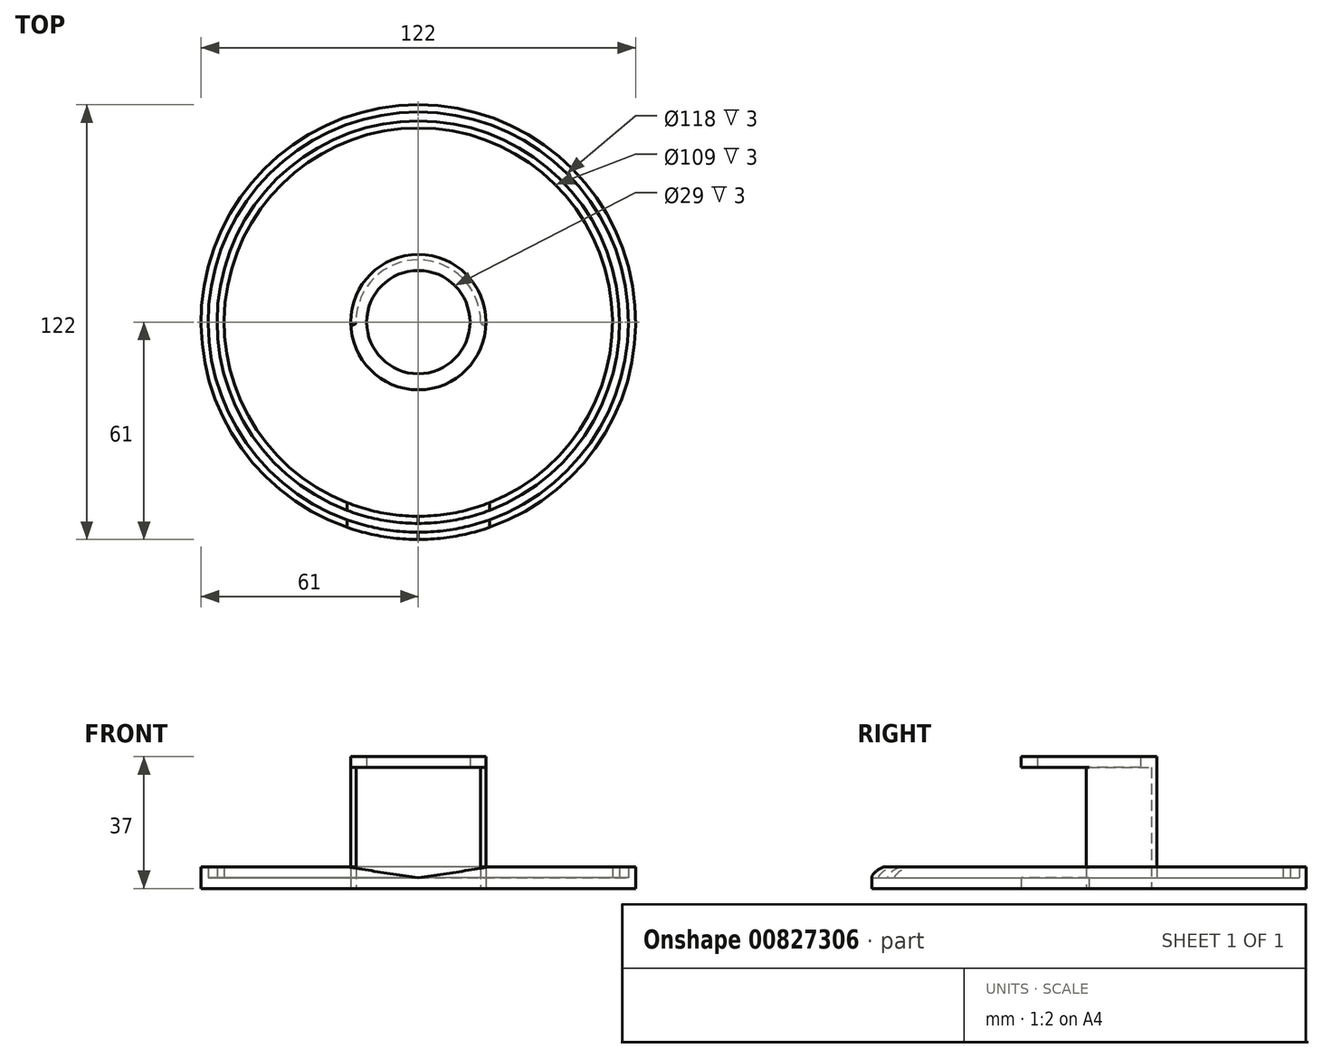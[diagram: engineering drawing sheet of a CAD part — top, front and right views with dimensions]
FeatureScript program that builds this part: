
annotation { "Feature Type Name" : "Feature", "Feature Type Description" : "" }
export const myFeature = defineFeature(function(context is Context, id is Id, definition is map)
    precondition{}
    {
        {
            var Q0;
            Q0=qCreatedBy(makeId("Top.planeOp"),FACE);
            var sketch = newSketch(context, id + "F0", { "sketchPlane" : qUnion([Q0])});
            skCircle(sketch, "E0", {"center": v(0, 0) * mm, "radius": 61 * mm});
            skCircle(sketch, "E1", {"center": v(0, 0) * mm, "radius": 11.5 * mm});
            skCircle(sketch, "E2", {"center": v(0, 0) * mm, "radius": 17.5 * mm});
            skCircle(sketch, "E3", {"center": v(0, 0) * mm, "radius": 14.5 * mm});
            skCircle(sketch, "E4", {"center": v(-18.25, 0) * mm, "radius": 0.75 * mm});
            skCircle(sketch, "E5", {"center": v(18.25, 0) * mm, "radius": 0.75 * mm});
            skCircle(sketch, "E6", {"center": v(0, 0) * mm, "radius": 19 * mm});
            skCircle(sketch, "E7", {"center": v(0, 0) * mm, "radius": 59 * mm});
            skCircle(sketch, "E8", {"center": v(0, 0) * mm, "radius": 56.5 * mm});
            skCircle(sketch, "E9", {"center": v(0, 0) * mm, "radius": 54.5 * mm});
            skSolve(sketch);
        }
        {
            var Q0;
            {var subQ0=sQuery(id+"F0.wireOp",EDGE,"E4");var subQ1=sQuery(id+"F0.wireOp",EDGE,"E2");var subQ2=makeQuery(id+"F0.imprint","INTERSECT",VERTEX,{"derivedFrom":[subQ1,subQ0]});Q0=makeQuery(id+"F0.imprint","IMPRINT",FACE,{"disambiguationData":[TD([[makeQuery(id+"F0.imprint","IMPRINT",EDGE,{"disambiguationData":[TD([[subQ2,1.0]])],"derivedFrom":subQ1}),-1.0]])]});}
            var Q1;
            {var subQ0=sQuery(id+"F0.wireOp",EDGE,"E5");var subQ1=makeQuery(id+"F0.imprint","INTERSECT",VERTEX,{"derivedFrom":[sQuery(id+"F0.wireOp",EDGE,"E2"),subQ0]});Q1=makeQuery(id+"F0.imprint","IMPRINT",FACE,{"disambiguationData":[TD([[makeQuery(id+"F0.imprint","IMPRINT",EDGE,{"disambiguationData":[TD([[subQ1,1.0]])],"derivedFrom":subQ0}),1.0]])]});}
            var Q2;
            {var subQ0=sQuery(id+"F0.wireOp",EDGE,"E4");var subQ1=makeQuery(id+"F0.imprint","INTERSECT",VERTEX,{"derivedFrom":[sQuery(id+"F0.wireOp",EDGE,"E2"),subQ0]});Q2=makeQuery(id+"F0.imprint","IMPRINT",FACE,{"disambiguationData":[TD([[makeQuery(id+"F0.imprint","IMPRINT",EDGE,{"disambiguationData":[TD([[subQ1,-1.0]])],"derivedFrom":subQ0}),1.0]])]});}
            extrude(context, id + "F1", {"entities" : qUnion([Q0, Q1, Q2]), "depth" : 34 * mm, "offsetDistance" : 25 * mm});
        }
        {
            var Q0;
            Q0=makeQuery(id+"F0.imprint","IMPRINT",FACE,{"disambiguationData":[TD([[makeQuery(id+"F0.imprint","IMPRINT",EDGE,{"derivedFrom":sQuery(id+"F0.wireOp",EDGE,"E0")}),1.0]])]});
            var Q1;
            Q1=makeQuery(id+"F0.imprint","IMPRINT",FACE,{"disambiguationData":[TD([[makeQuery(id+"F0.imprint","IMPRINT",EDGE,{"derivedFrom":sQuery(id+"F0.wireOp",EDGE,"E7")}),1.0]])]});
            var Q2;
            Q2=makeQuery(id+"F0.imprint","IMPRINT",FACE,{"disambiguationData":[TD([[makeQuery(id+"F0.imprint","IMPRINT",EDGE,{"derivedFrom":sQuery(id+"F0.wireOp",EDGE,"E8")}),1.0]])]});
            var Q3;
            Q3=makeQuery(id+"F0.imprint","IMPRINT",FACE,{"disambiguationData":[TD([[makeQuery(id+"F0.imprint","IMPRINT",EDGE,{"derivedFrom":sQuery(id+"F0.wireOp",EDGE,"E9")}),1.0]])]});
            extrude(context, id + "F2", {"entities" : qUnion([Q0, Q1, Q2, Q3]), "operationType" : NewBodyOperationType.ADD, "depth" : 3 * mm, "offsetDistance" : 25 * mm});
        }
        {
            var Q0;
            Q0=makeQuery(id+"F0.imprint","IMPRINT",FACE,{"disambiguationData":[TD([[makeQuery(id+"F0.imprint","IMPRINT",EDGE,{"derivedFrom":sQuery(id+"F0.wireOp",EDGE,"E3")}),-1.0]])]});
            var Q1;
            {var subQ0=sQuery(id+"F0.wireOp",EDGE,"E4");var subQ1=sQuery(id+"F0.wireOp",EDGE,"E2");var subQ2=makeQuery(id+"F0.imprint","INTERSECT",VERTEX,{"derivedFrom":[subQ1,subQ0]});Q1=makeQuery(id+"F0.imprint","IMPRINT",FACE,{"disambiguationData":[TD([[makeQuery(id+"F0.imprint","IMPRINT",EDGE,{"disambiguationData":[TD([[subQ2,1.0]])],"derivedFrom":subQ1}),-1.0]])]});}
            var Q2;
            {var subQ0=sQuery(id+"F0.wireOp",EDGE,"E5");var subQ1=makeQuery(id+"F0.imprint","INTERSECT",VERTEX,{"derivedFrom":[sQuery(id+"F0.wireOp",EDGE,"E2"),subQ0]});Q2=makeQuery(id+"F0.imprint","IMPRINT",FACE,{"disambiguationData":[TD([[makeQuery(id+"F0.imprint","IMPRINT",EDGE,{"disambiguationData":[TD([[subQ1,1.0]])],"derivedFrom":subQ0}),1.0]])]});}
            var Q3;
            {var subQ0=sQuery(id+"F0.wireOp",EDGE,"E4");var subQ1=makeQuery(id+"F0.imprint","INTERSECT",VERTEX,{"derivedFrom":[sQuery(id+"F0.wireOp",EDGE,"E2"),subQ0]});Q3=makeQuery(id+"F0.imprint","IMPRINT",FACE,{"disambiguationData":[TD([[makeQuery(id+"F0.imprint","IMPRINT",EDGE,{"disambiguationData":[TD([[subQ1,-1.0]])],"derivedFrom":subQ0}),1.0]])]});}
            var Q4;
            {var subQ0=sQuery(id+"F0.wireOp",EDGE,"E4");var subQ1=sQuery(id+"F0.wireOp",EDGE,"E2");var subQ2=makeQuery(id+"F0.imprint","INTERSECT",VERTEX,{"derivedFrom":[subQ1,subQ0]});Q4=makeQuery(id+"F0.imprint","IMPRINT",FACE,{"disambiguationData":[TD([[makeQuery(id+"F0.imprint","IMPRINT",EDGE,{"disambiguationData":[TD([[subQ2,-1.0]])],"derivedFrom":subQ1}),-1.0]])]});}
            extrude(context, id + "F3", {"entities" : qUnion([Q0, Q1, Q2, Q3, Q4]), "operationType" : NewBodyOperationType.ADD, "depth" : 37 * mm, "offsetDistance" : 25 * mm, "hasSecondDirection" : true, "secondDirectionOppositeDirection" : false, "secondDirectionDepth" : 34 * mm});
        }
        {
            var Q0;
            Q0=makeQuery(id+"F0.imprint","IMPRINT",FACE,{"disambiguationData":[TD([[makeQuery(id+"F0.imprint","IMPRINT",EDGE,{"derivedFrom":sQuery(id+"F0.wireOp",EDGE,"E0")}),1.0]])]});
            var Q1;
            Q1=makeQuery(id+"F0.imprint","IMPRINT",FACE,{"disambiguationData":[TD([[makeQuery(id+"F0.imprint","IMPRINT",EDGE,{"derivedFrom":sQuery(id+"F0.wireOp",EDGE,"E8")}),1.0]])]});
            extrude(context, id + "F4", {"entities" : qUnion([Q0, Q1]), "operationType" : NewBodyOperationType.ADD, "depth" : 6 * mm, "offsetDistance" : 25 * mm});
        }
        {
            var Q0;
            Q0=qCreatedBy(makeId("Front.planeOp"),FACE);
            var sketch = newSketch(context, id + "F5", { "sketchPlane" : qUnion([Q0])});
            skPoint(sketch, "E10", {"position": v(0, 3) * mm});
            skLineSegment(sketch, "E11", {"start": v(0, 3) * mm, "end": v(0, 6) * mm});
            skLineSegment(sketch, "E12", {"start": v(0, 6) * mm, "end": v(-20, 6) * mm});
            skLineSegment(sketch, "E13", {"start": v(0, 6) * mm, "end": v(20, 6) * mm});
            skLineSegment(sketch, "E14", {"start": v(-20, 6) * mm, "end": v(0, 3) * mm});
            skLineSegment(sketch, "E15", {"start": v(0, 3) * mm, "end": v(20, 6) * mm});
            skSolve(sketch);
        }
        {
            var Q0;
            Q0=makeQuery(id+"F5.imprint","IMPRINT",FACE,{"disambiguationData":[TD([[makeQuery(id+"F5.imprint","IMPRINT",EDGE,{"derivedFrom":sQuery(id+"F5.wireOp",EDGE,"E11")}),1.0]])]});
            var Q1;
            Q1=makeQuery(id+"F5.imprint","IMPRINT",FACE,{"disambiguationData":[TD([[makeQuery(id+"F5.imprint","IMPRINT",EDGE,{"derivedFrom":sQuery(id+"F5.wireOp",EDGE,"E11")}),-1.0]])]});
            extrude(context, id + "F6", {"entities" : qUnion([Q0, Q1]), "operationType" : NewBodyOperationType.REMOVE, "endBound" : BoundingType.THROUGH_ALL, "depth" : 25 * mm, "offsetDistance" : 25 * mm});
        }
    });
